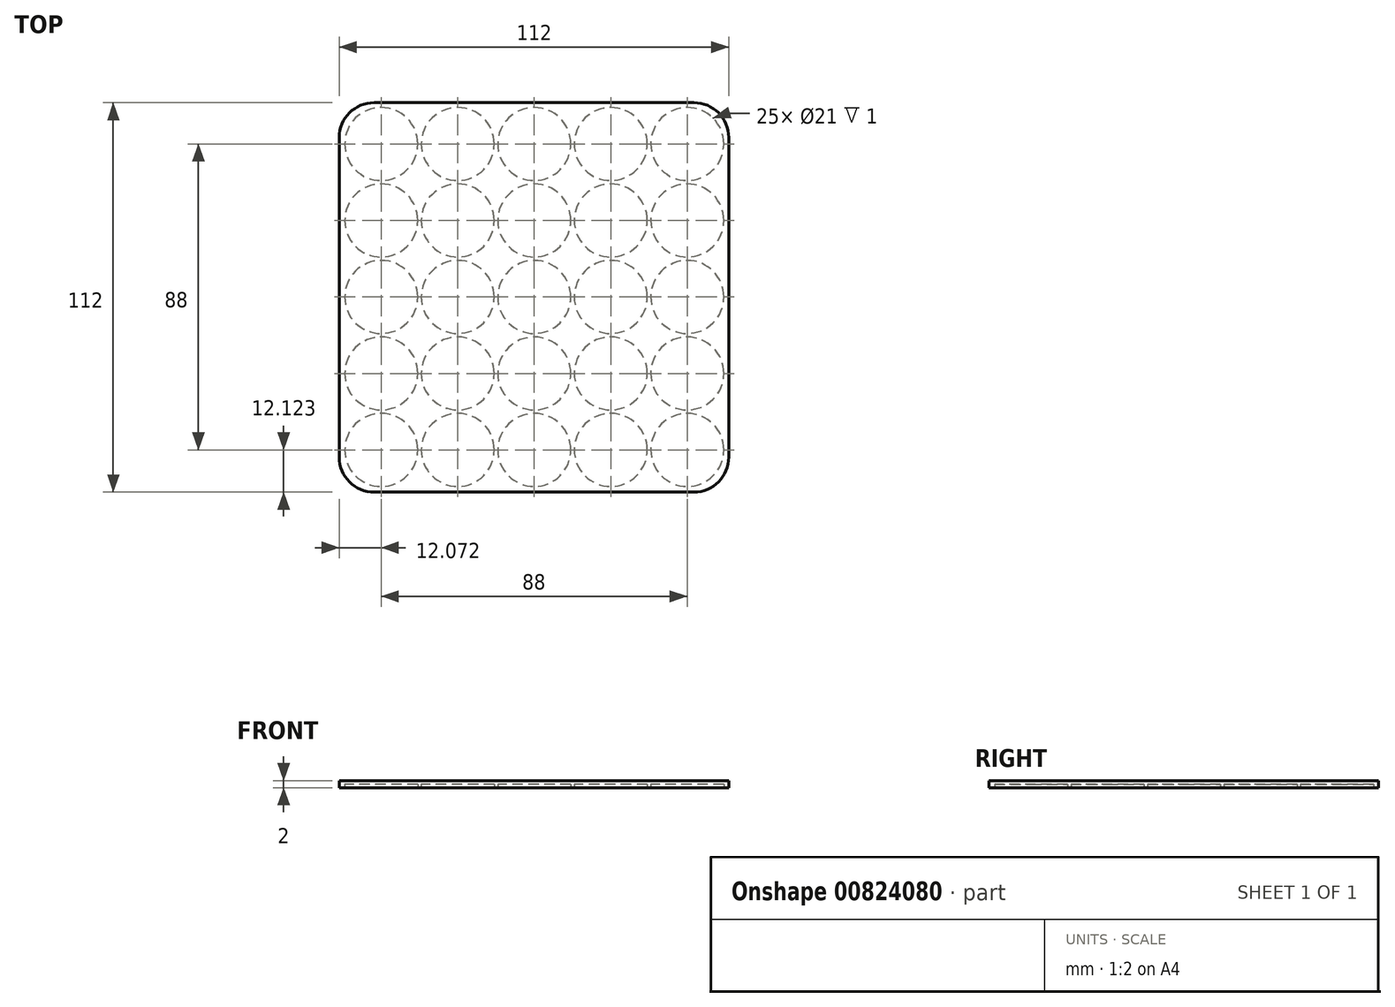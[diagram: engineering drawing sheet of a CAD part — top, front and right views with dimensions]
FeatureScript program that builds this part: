
annotation { "Feature Type Name" : "Feature", "Feature Type Description" : "" }
export const myFeature = defineFeature(function(context is Context, id is Id, definition is map)
    precondition{}
    {
        {
            var Q0;
            Q0=qCreatedBy(makeId("Top.planeOp"),FACE);
            var sketch = newSketch(context, id + "F0", { "sketchPlane" : qUnion([Q0])});
            skCircle(sketch, "E0", {"center": v(-214.9, -61.8) * mm, "radius": 10.5 * mm});
            skCircle(sketch, "E1.0.1.0", {"center": v(-214.9, -39.8) * mm, "radius": 10.5 * mm});
            skCircle(sketch, "E1.0.2.0", {"center": v(-214.9, -17.8) * mm, "radius": 10.5 * mm});
            skCircle(sketch, "E1.0.3.0", {"center": v(-214.9, 4.2) * mm, "radius": 10.5 * mm});
            skCircle(sketch, "E1.0.4.0", {"center": v(-214.9, 26.2) * mm, "radius": 10.5 * mm});
            skCircle(sketch, "E1.1.0.0", {"center": v(-192.9, -61.8) * mm, "radius": 10.5 * mm});
            skCircle(sketch, "E1.1.1.0", {"center": v(-192.9, -39.8) * mm, "radius": 10.5 * mm});
            skCircle(sketch, "E1.1.2.0", {"center": v(-192.9, -17.8) * mm, "radius": 10.5 * mm});
            skCircle(sketch, "E1.1.3.0", {"center": v(-192.9, 4.2) * mm, "radius": 10.5 * mm});
            skCircle(sketch, "E1.1.4.0", {"center": v(-192.9, 26.2) * mm, "radius": 10.5 * mm});
            skCircle(sketch, "E1.2.0.0", {"center": v(-170.9, -61.8) * mm, "radius": 10.5 * mm});
            skCircle(sketch, "E1.2.1.0", {"center": v(-170.9, -39.8) * mm, "radius": 10.5 * mm});
            skCircle(sketch, "E1.2.2.0", {"center": v(-170.9, -17.8) * mm, "radius": 10.5 * mm});
            skCircle(sketch, "E1.2.3.0", {"center": v(-170.9, 4.2) * mm, "radius": 10.5 * mm});
            skCircle(sketch, "E1.2.4.0", {"center": v(-170.9, 26.2) * mm, "radius": 10.5 * mm});
            skCircle(sketch, "E1.3.0.0", {"center": v(-148.9, -61.8) * mm, "radius": 10.5 * mm});
            skCircle(sketch, "E1.3.1.0", {"center": v(-148.9, -39.8) * mm, "radius": 10.5 * mm});
            skCircle(sketch, "E1.3.2.0", {"center": v(-148.9, -17.8) * mm, "radius": 10.5 * mm});
            skCircle(sketch, "E1.3.3.0", {"center": v(-148.9, 4.2) * mm, "radius": 10.5 * mm});
            skCircle(sketch, "E1.3.4.0", {"center": v(-148.9, 26.2) * mm, "radius": 10.5 * mm});
            skCircle(sketch, "E1.4.0.0", {"center": v(-126.9, -61.8) * mm, "radius": 10.5 * mm});
            skCircle(sketch, "E1.4.1.0", {"center": v(-126.9, -39.8) * mm, "radius": 10.5 * mm});
            skCircle(sketch, "E1.4.2.0", {"center": v(-126.9, -17.8) * mm, "radius": 10.5 * mm});
            skCircle(sketch, "E1.4.3.0", {"center": v(-126.9, 4.2) * mm, "radius": 10.5 * mm});
            skCircle(sketch, "E1.4.4.0", {"center": v(-126.9, 26.2) * mm, "radius": 10.5 * mm});
            skLineSegment(sketch, "E1.direction1", {"start": v(-214.9, -61.8) * mm, "end": v(-192.9, -61.8) * mm, "construction": true});
            skLineSegment(sketch, "E1.direction2", {"start": v(-214.9, -61.8) * mm, "end": v(-214.9, -39.8) * mm, "construction": true});
            skLineSegment(sketch, "E2.bottom", {"start": v(-124.97, 38.07) * mm, "end": v(-216.97, 38.07) * mm});
            skLineSegment(sketch, "E2.top", {"start": v(-124.97, -73.93) * mm, "end": v(-216.97, -73.93) * mm});
            skLineSegment(sketch, "E2.left", {"start": v(-114.97, 28.07) * mm, "end": v(-114.97, -63.93) * mm});
            skLineSegment(sketch, "E2.right", {"start": v(-226.97, 28.07) * mm, "end": v(-226.97, -63.93) * mm});
            skPoint(sketch, "E3.visualSharp", {"position": v(-226.97, -73.93) * mm});
            skArc(sketch, "E3.filletArc", {"start": v(-226.97, -63.93) * mm, "mid": v(-224.05, -71) * mm, "end": v(-216.97, -73.93) * mm});
            skPoint(sketch, "E4.visualSharp", {"position": v(-114.97, -73.93) * mm});
            skArc(sketch, "E4.filletArc", {"start": v(-124.97, -73.93) * mm, "mid": v(-117.9, -71) * mm, "end": v(-114.97, -63.93) * mm});
            skPoint(sketch, "E5.visualSharp", {"position": v(-114.97, 38.07) * mm});
            skArc(sketch, "E5.filletArc", {"start": v(-114.97, 28.07) * mm, "mid": v(-117.9, 35.15) * mm, "end": v(-124.97, 38.07) * mm});
            skPoint(sketch, "E6.visualSharp", {"position": v(-226.97, 38.07) * mm});
            skArc(sketch, "E6.filletArc", {"start": v(-216.97, 38.07) * mm, "mid": v(-224.05, 35.15) * mm, "end": v(-226.97, 28.07) * mm});
            skSolve(sketch);
        }
        {
            var Q0;
            Q0=makeQuery(id+"F0.imprint","IMPRINT",FACE,{"disambiguationData":[TD([[makeQuery(id+"F0.imprint","IMPRINT",EDGE,{"derivedFrom":sQuery(id+"F0.wireOp",EDGE,"E2.bottom")}),1.0]])]});
            extrude(context, id + "F1", {"entities" : qUnion([Q0]), "depth" : 1 * mm, "offsetDistance" : 25 * mm});
        }
        {
            var Q0;
            Q0=makeQuery(id+"F1.opExtrude","CAP_FACE",FACE,{"disambiguationData":[OSD([sQuery(id+"F0.wireOp",EDGE,"E0"),sQuery(id+"F0.wireOp",EDGE,"E1.0.1.0"),sQuery(id+"F0.wireOp",EDGE,"E1.0.2.0"),sQuery(id+"F0.wireOp",EDGE,"E1.0.3.0"),sQuery(id+"F0.wireOp",EDGE,"E1.0.4.0"),sQuery(id+"F0.wireOp",EDGE,"E1.1.0.0"),sQuery(id+"F0.wireOp",EDGE,"E1.1.1.0"),sQuery(id+"F0.wireOp",EDGE,"E1.1.2.0"),sQuery(id+"F0.wireOp",EDGE,"E1.1.3.0"),sQuery(id+"F0.wireOp",EDGE,"E1.1.4.0"),sQuery(id+"F0.wireOp",EDGE,"E1.2.0.0"),sQuery(id+"F0.wireOp",EDGE,"E1.2.1.0"),sQuery(id+"F0.wireOp",EDGE,"E1.2.2.0"),sQuery(id+"F0.wireOp",EDGE,"E1.2.3.0"),sQuery(id+"F0.wireOp",EDGE,"E1.2.4.0"),sQuery(id+"F0.wireOp",EDGE,"E1.3.0.0"),sQuery(id+"F0.wireOp",EDGE,"E1.3.1.0"),sQuery(id+"F0.wireOp",EDGE,"E1.3.2.0"),sQuery(id+"F0.wireOp",EDGE,"E1.3.3.0"),sQuery(id+"F0.wireOp",EDGE,"E1.3.4.0"),sQuery(id+"F0.wireOp",EDGE,"E1.4.0.0"),sQuery(id+"F0.wireOp",EDGE,"E1.4.1.0"),sQuery(id+"F0.wireOp",EDGE,"E1.4.2.0"),sQuery(id+"F0.wireOp",EDGE,"E1.4.3.0"),sQuery(id+"F0.wireOp",EDGE,"E1.4.4.0"),sQuery(id+"F0.wireOp",EDGE,"E2.bottom"),sQuery(id+"F0.wireOp",EDGE,"E2.top"),sQuery(id+"F0.wireOp",EDGE,"E2.left"),sQuery(id+"F0.wireOp",EDGE,"E2.right"),sQuery(id+"F0.wireOp",EDGE,"E3.filletArc"),sQuery(id+"F0.wireOp",EDGE,"E4.filletArc"),sQuery(id+"F0.wireOp",EDGE,"E5.filletArc"),sQuery(id+"F0.wireOp",EDGE,"E6.filletArc")])],"isStart":false});
            var sketch = newSketch(context, id + "F2", { "sketchPlane" : qUnion([Q0])});
            skLineSegment(sketch, "E7.0", {"start": v(-124.97, 38.07) * mm, "end": v(-216.97, 38.07) * mm});
            skArc(sketch, "E7.1", {"start": v(-216.97, 38.07) * mm, "mid": v(-224.05, 35.15) * mm, "end": v(-226.97, 28.07) * mm});
            skLineSegment(sketch, "E7.2", {"start": v(-226.97, 28.07) * mm, "end": v(-226.97, -63.93) * mm});
            skArc(sketch, "E7.3", {"start": v(-226.97, -63.93) * mm, "mid": v(-224.05, -71) * mm, "end": v(-216.97, -73.93) * mm});
            skLineSegment(sketch, "E7.4", {"start": v(-124.97, -73.93) * mm, "end": v(-216.97, -73.93) * mm});
            skArc(sketch, "E7.5", {"start": v(-124.97, -73.93) * mm, "mid": v(-117.9, -71) * mm, "end": v(-114.97, -63.93) * mm});
            skLineSegment(sketch, "E7.6", {"start": v(-114.97, 28.07) * mm, "end": v(-114.97, -63.93) * mm});
            skArc(sketch, "E7.7", {"start": v(-114.97, 28.07) * mm, "mid": v(-117.9, 35.15) * mm, "end": v(-124.97, 38.07) * mm});
            skSolve(sketch);
        }
        {
            var Q0;
            Q0 = qSketchRegion(id + "F2", true);
            var Q1;
            Q1=makeQuery(id+"F2.imprint","IMPRINT",FACE,{"disambiguationData":[TD([[makeQuery(id+"F2.imprint","IMPRINT",EDGE,{"derivedFrom":sQuery(id+"F2.wireOp",EDGE,"E7.0")}),1.0]])]});
            extrude(context, id + "F3", {"entities" : qUnion([Q0, Q1]), "operationType" : NewBodyOperationType.ADD, "depth" : 1 * mm, "offsetDistance" : 25 * mm});
        }
    });
